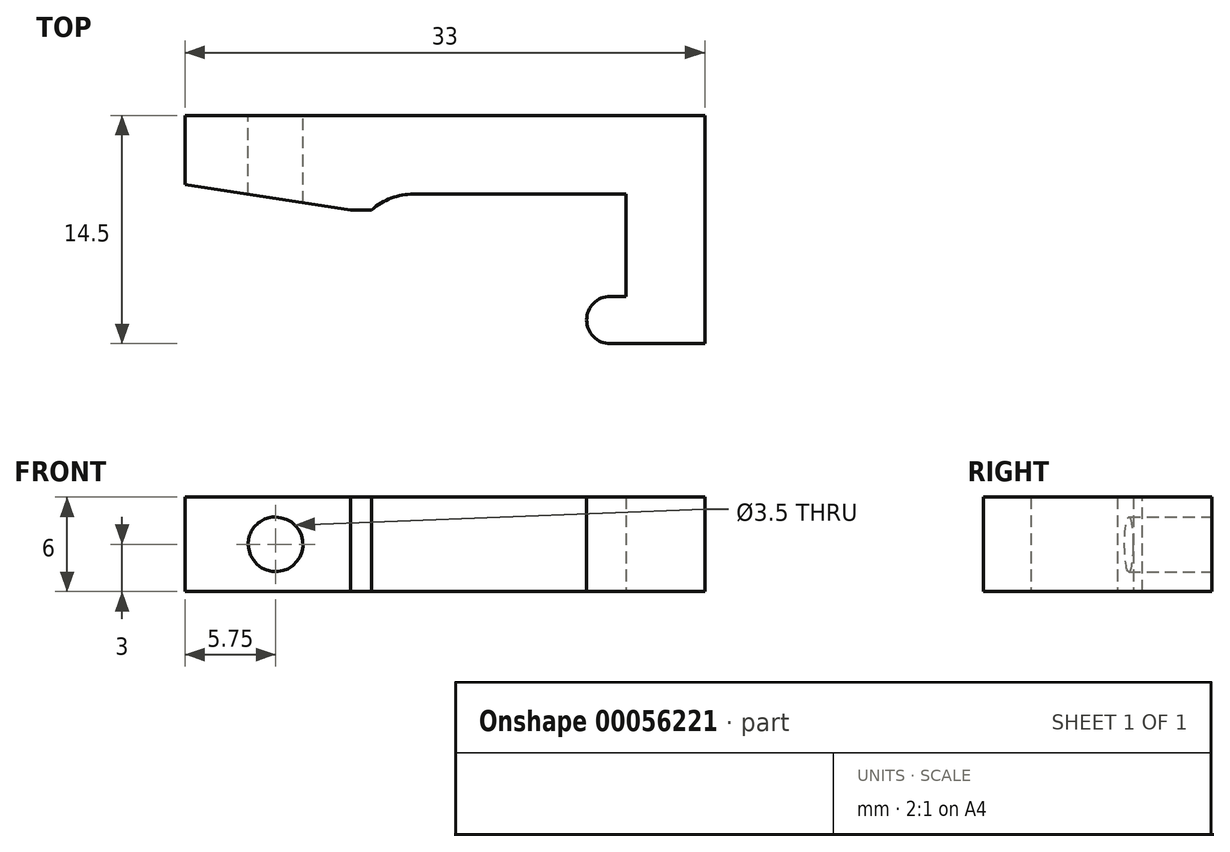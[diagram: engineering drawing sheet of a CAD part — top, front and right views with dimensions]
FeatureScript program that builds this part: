
annotation { "Feature Type Name" : "Feature", "Feature Type Description" : "" }
export const myFeature = defineFeature(function(context is Context, id is Id, definition is map)
    precondition{}
    {
        {
            var Q0;
            Q0=qCreatedBy(makeId("Top.planeOp"),FACE);
            var sketch = newSketch(context, id + "F0", { "sketchPlane" : qUnion([Q0])});
            skLineSegment(sketch, "E0", {"start": v(0, 0) * mm, "end": v(5, 0) * mm});
            skLineSegment(sketch, "E1", {"start": v(5, 0) * mm, "end": v(5, 14.5) * mm});
            skLineSegment(sketch, "E2", {"start": v(5, 14.5) * mm, "end": v(-28, 14.5) * mm});
            skLineSegment(sketch, "E3", {"start": v(-28, 14.5) * mm, "end": v(-28, 9.5) * mm});
            skLineSegment(sketch, "E4", {"start": v(-28, 9.5) * mm, "end": v(0, 9.5) * mm});
            skLineSegment(sketch, "E5", {"start": v(0, 9.5) * mm, "end": v(0, 3) * mm});
            skLineSegment(sketch, "E6", {"start": v(0, 3) * mm, "end": v(-1, 3) * mm});
            skLineSegment(sketch, "E7", {"start": v(0, 0) * mm, "end": v(-1, 0) * mm});
            skArc(sketch, "E8", {"start": v(-1, 3) * mm, "mid": v(-2.5, 1.5) * mm, "end": v(-1, 0) * mm});
            skPoint(sketch, "E9.oppositeSnap0", {"position": v(0, 8.5) * mm});
            skLineSegment(sketch, "E9.bottom", {"start": v(0, 9.5) * mm, "end": v(-28, 9.5) * mm});
            skLineSegment(sketch, "E9.top", {"start": v(0, 8.5) * mm, "end": v(-28, 8.5) * mm});
            skLineSegment(sketch, "E9.left", {"start": v(0, 9.5) * mm, "end": v(0, 8.5) * mm});
            skLineSegment(sketch, "E9.right", {"start": v(-28, 9.5) * mm, "end": v(-28, 8.5) * mm});
            skCircle(sketch, "E10", {"center": v(-13.5, 5.5) * mm, "radius": 4 * mm});
            skSolve(sketch);
        }
        {
            var Q0;
            Q0=makeQuery(id+"F0.imprint","IMPRINT",FACE,{"disambiguationData":[TD([[makeQuery(id+"F0.imprint","IMPRINT",EDGE,{"derivedFrom":sQuery(id+"F0.wireOp",EDGE,"E0")}),1.0]])]});
            var Q1;
            {var subQ0=sQuery(id+"F0.wireOp",EDGE,"E9.left");Q1=makeQuery(id+"F0.imprint","IMPRINT",FACE,{"disambiguationData":[TD([[makeQuery(id+"F0.imprint","IMPRINT",EDGE,{"derivedFrom":subQ0}),-1.0]])]});}
            var Q2;
            {var subQ0=sQuery(id+"F0.wireOp",EDGE,"E9.right");Q2=makeQuery(id+"F0.imprint","IMPRINT",FACE,{"disambiguationData":[TD([[makeQuery(id+"F0.imprint","IMPRINT",EDGE,{"derivedFrom":subQ0}),1.0]])]});}
            extrude(context, id + "F1", {"entities" : qUnion([Q0, Q1, Q2]), "depth" : 6 * mm, "offsetDistance" : 25 * mm});
        }
        {
            var Q0;
            Q0=makeQuery(id+"F1.opExtrude","SWEPT_FACE",FACE,{"disambiguationData":[OSD([sQuery(id+"F0.wireOp",EDGE,"E2")])]});
            var sketch = newSketch(context, id + "F2", { "sketchPlane" : qUnion([Q0])});
            skCircle(sketch, "E11", {"center": v(22.25, 3) * mm, "radius": 1.75 * mm});
            skLineSegment(sketch, "E12", {"start": v(22.25, 6) * mm, "end": v(22.25, 0) * mm});
            skSolve(sketch);
        }
        {
            var Q0;
            Q0=qSketchRegion(id+"F2",true);
            var Q1;
            {var subQ0=sQuery(id+"F2.wireOp",EDGE,"48912eb0-2b95-4dd2-85f4-164080705240");var subQ1=sQuery(id+"F2.wireOp",EDGE,"E11");var subQ3=makeQuery(id+"F2.imprint","INTERSECT",VERTEX,{"disambiguationData":[OD(0.0)],"derivedFrom":[subQ1,subQ0]});Q1=makeQuery(id+"F2.imprint","IMPRINT",FACE,{"disambiguationData":[TD([[makeQuery(id+"F2.imprint","IMPRINT",EDGE,{"disambiguationData":[TD([[subQ3,-1.0]])],"derivedFrom":subQ1}),1.0]])]});}
            extrude(context, id + "F3", {"entities" : qUnion([Q0, Q1]), "operationType" : NewBodyOperationType.REMOVE, "oppositeDirection" : true, "depth" : 25 * mm});
        }
        {
            var Q0;
            Q0=makeQuery(id+"F1.opExtrude","SWEPT_EDGE",EDGE,{"disambiguationData":[OSD([sQuery(id+"F0.wireOp",EDGE,"E9.top"),sQuery(id+"F0.wireOp",EDGE,"E9.right")])]});
            chamfer(context, id + "F4", {"entities" : qUnion([Q0]), "chamferType" : ChamferType.TWO_OFFSETS, "width1" : 10.5 * mm, "oppositeDirection" : false, "width2" : 1.6 * mm, "tangentPropagation" : true});
        }
    });
